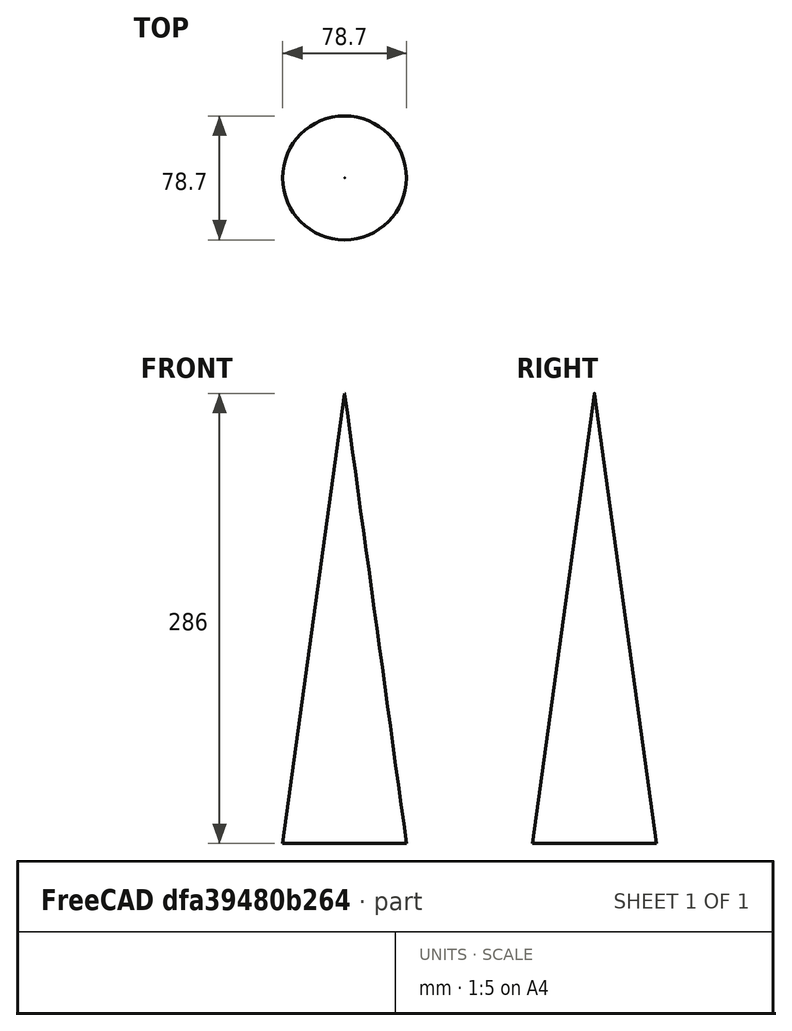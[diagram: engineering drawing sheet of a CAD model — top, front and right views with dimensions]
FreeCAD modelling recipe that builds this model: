
FCSTD DOCUMENT  (FreeCAD 1.0R39285 (Git))
Label: Nosecone
License: All rights reserved
LicenseURL: https://en.wikipedia.org/wiki/All_rights_reserved
objects: Sketcher::SketchObject×1, PartDesign::Pad×1, PartDesign::Body×1
note: 6 computed .brp shape members not serialized (recipe doc carries the construction recipe); baked Part::Feature solids carry a one-line shape summary decoded from their .brp

FEATURE [Sketcher::SketchObject] Sketch
  ArcFitTolerance = 1e-06
  AttachmentSupport = -> [XY_Plane]
  FullyConstrained = true
  MakeInternals = false
  MapMode = 5
  sketch-geometry (1):
    g0: Circle CenterX=0 CenterY=0 CenterZ=0 NormalX=0 NormalY=0 NormalZ=1 AngleXU=0 Radius=39.35
  constraints (2):
    c: Diameter(g0) = 78.7
    c: Coincident(g0,g-1)
FEATURE [PartDesign::Pad] Pad
  Direction = (0,0,1)
  Length = 286
  Length2 = 10
  Profile = -> Sketch
  ReferenceAxis = -> Sketch [N_Axis]
  Refine = true
  Suppressed = false
  TaperAngle = -7.83
  Type = 0
FEATURE [PartDesign::Body] Body
  AllowCompound = false
  Group = -> [Sketch,Pad]
  Origin = -> Origin
  Tip = -> Pad
